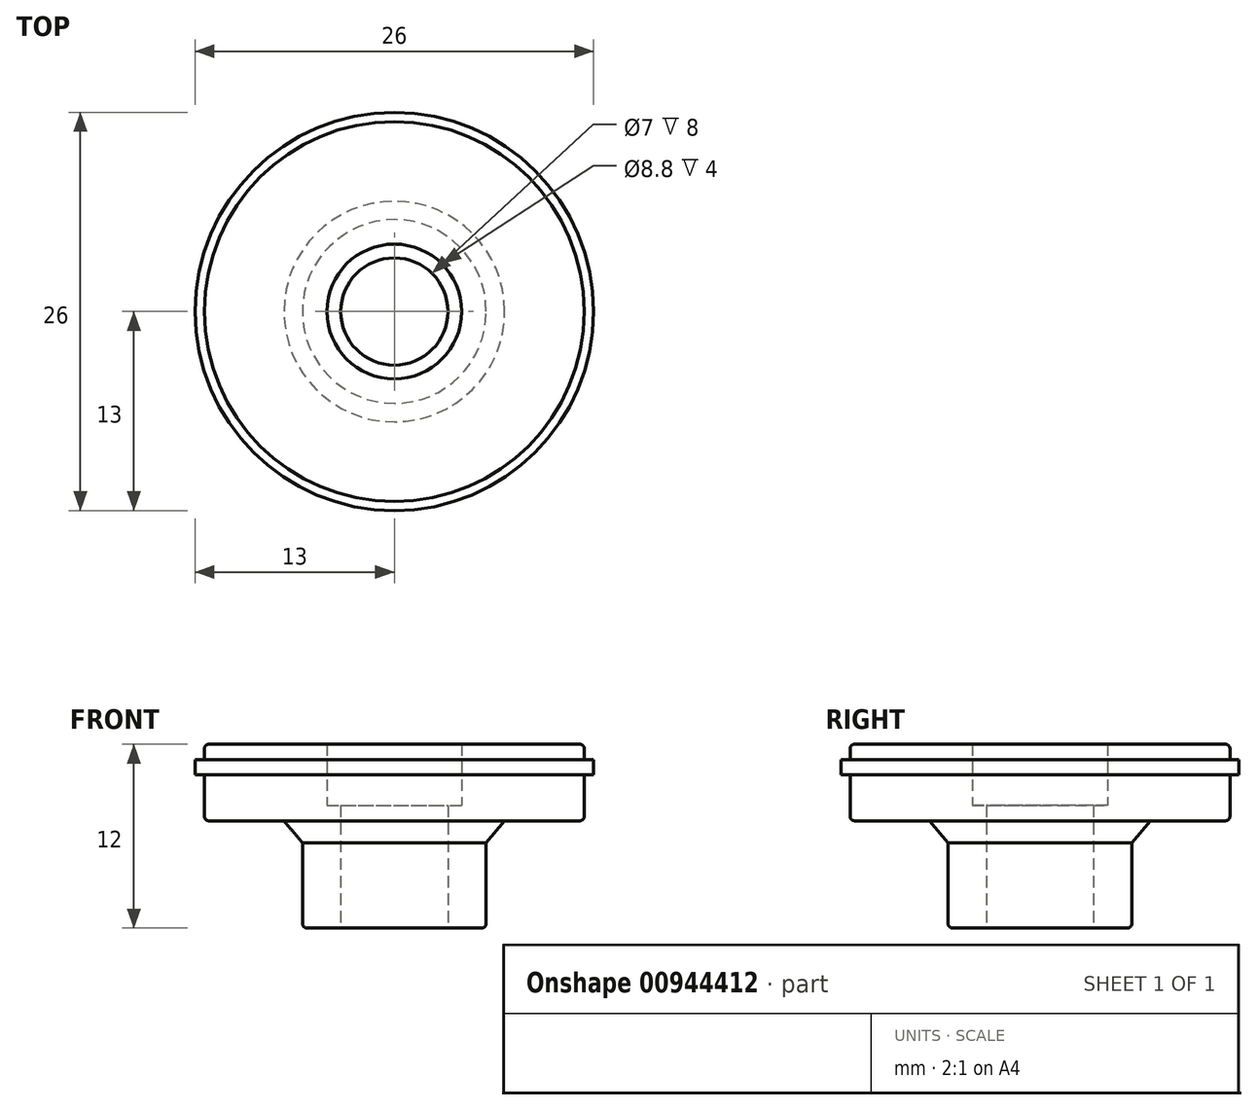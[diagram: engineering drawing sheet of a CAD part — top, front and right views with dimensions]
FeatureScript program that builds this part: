
annotation { "Feature Type Name" : "Feature", "Feature Type Description" : "" }
export const myFeature = defineFeature(function(context is Context, id is Id, definition is map)
    precondition{}
    {
        {
            var Q0;
            Q0=qCreatedBy(makeId("Front.planeOp"),FACE);
            var sketch = newSketch(context, id + "F0", { "sketchPlane" : qUnion([Q0])});
            skLineSegment(sketch, "E0", {"start": v(0, 0) * mm, "end": v(0, 14.94) * mm, "construction": true});
            skLineSegment(sketch, "E1", {"start": v(-3.5, 0) * mm, "end": v(-6, 0) * mm});
            skLineSegment(sketch, "E2", {"start": v(-6, 0) * mm, "end": v(-6, 5.55) * mm});
            skLineSegment(sketch, "E3", {"start": v(-7.2, 7) * mm, "end": v(-12.4, 7) * mm});
            skLineSegment(sketch, "E4", {"start": v(-12.4, 7) * mm, "end": v(-12.4, 10) * mm});
            skLineSegment(sketch, "E5", {"start": v(-12.4, 10) * mm, "end": v(-13, 10) * mm});
            skLineSegment(sketch, "E6", {"start": v(-13, 10) * mm, "end": v(-13, 11) * mm});
            skLineSegment(sketch, "E7", {"start": v(-13, 11) * mm, "end": v(-12.4, 11) * mm});
            skLineSegment(sketch, "E8", {"start": v(-12.4, 11) * mm, "end": v(-12.4, 12) * mm});
            skLineSegment(sketch, "E9", {"start": v(-12.4, 12) * mm, "end": v(-4.4, 12) * mm});
            skLineSegment(sketch, "E10", {"start": v(-4.4, 12) * mm, "end": v(-4.4, 8) * mm});
            skLineSegment(sketch, "E11", {"start": v(-4.4, 8) * mm, "end": v(-3.5, 8) * mm});
            skLineSegment(sketch, "E12", {"start": v(-3.5, 8) * mm, "end": v(-3.5, 0) * mm});
            skLineSegment(sketch, "E13", {"start": v(-7.2, 7) * mm, "end": v(-6, 5.55) * mm});
            skSolve(sketch);
        }
        {
            var Q0;
            Q0=makeQuery(id+"F0.imprint","IMPRINT",FACE,{"disambiguationData":[TD([[makeQuery(id+"F0.imprint","IMPRINT",EDGE,{"derivedFrom":sQuery(id+"F0.wireOp",EDGE,"E1")}),-1.0]])]});
            var Q1;
            Q1=sQuery(id+"F0.wireOp",EDGE,"E0");
            revolve(context, id + "F1", {"surfaceOperationType" : NewSurfaceOperationType.NEW, "entities" : qUnion([Q0]), "axis" : qUnion([Q1]), "revolveType" : RevolveType.FULL});
        }
        {
            var Q0;
            Q0=makeQuery(id+"F1.opRevolve","SWEPT_EDGE",EDGE,{"disambiguationData":[OSD([sQuery(id+"F0.wireOp",EDGE,"E8"),sQuery(id+"F0.wireOp",EDGE,"E9")])]});
            var Q1;
            Q1=makeQuery(id+"F1.opRevolve","SWEPT_EDGE",EDGE,{"disambiguationData":[OSD([sQuery(id+"F0.wireOp",EDGE,"E3"),sQuery(id+"F0.wireOp",EDGE,"E4")])]});
            var Q2;
            Q2=makeQuery(id+"F1.opRevolve","SWEPT_EDGE",EDGE,{"disambiguationData":[OSD([sQuery(id+"F0.wireOp",EDGE,"E1"),sQuery(id+"F0.wireOp",EDGE,"E2")])]});
            fillet(context, id + "F2", {"entities" : qUnion([Q0, Q1, Q2]), "radius" : 0.3 * mm, "tangentPropagation" : true, "allowEdgeOverflow" : false});
        }
    });
